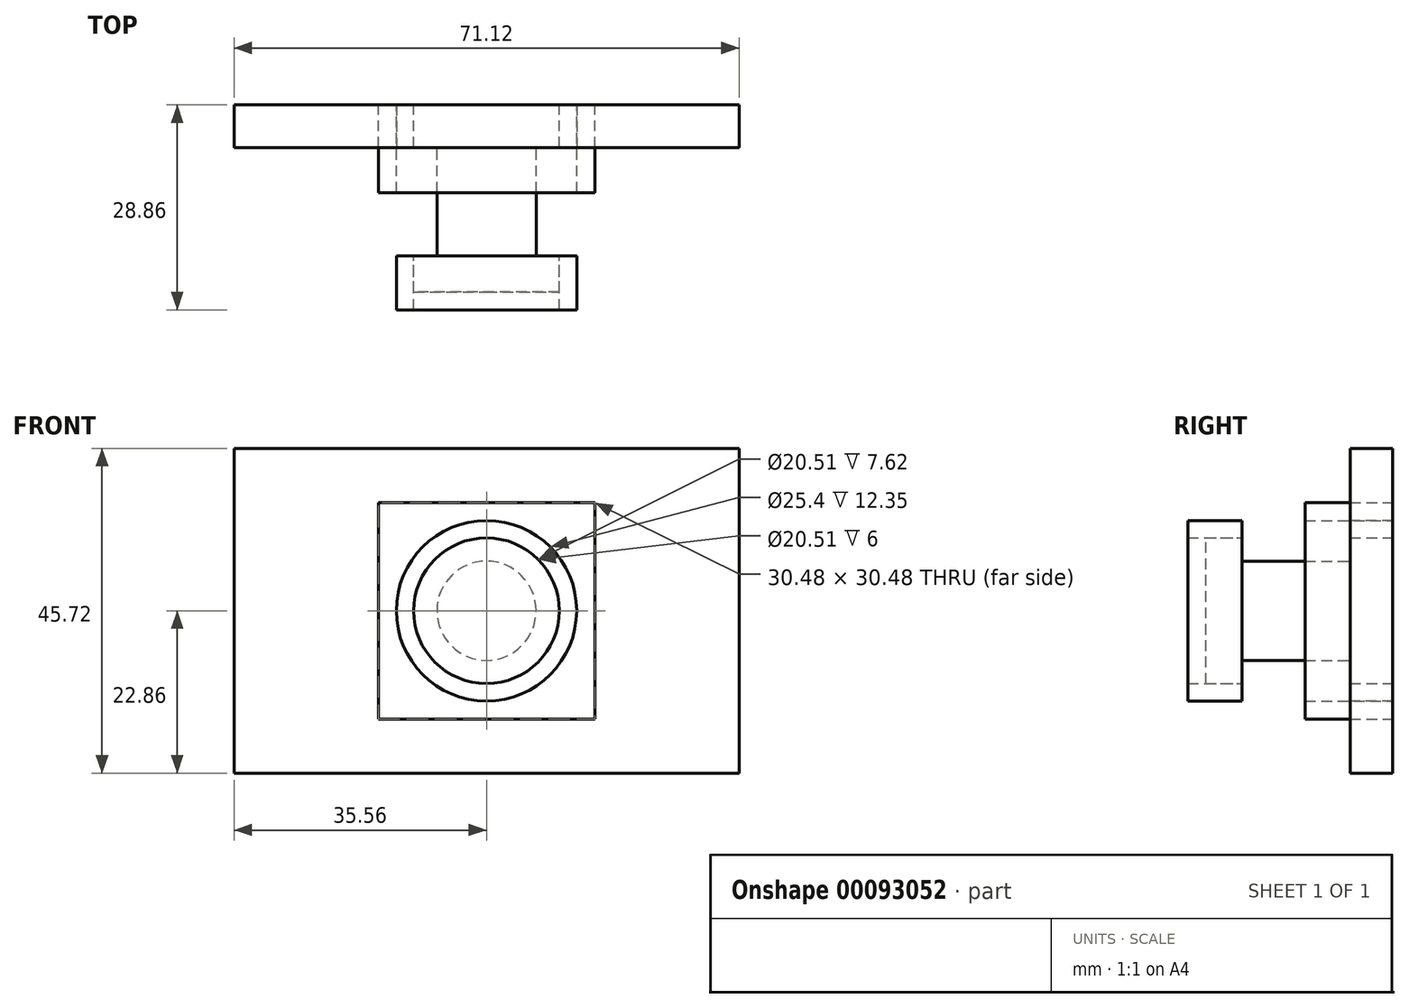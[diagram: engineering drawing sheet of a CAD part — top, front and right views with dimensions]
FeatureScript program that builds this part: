
annotation { "Feature Type Name" : "Feature", "Feature Type Description" : "" }
export const myFeature = defineFeature(function(context is Context, id is Id, definition is map)
    precondition{}
    {
        {
            var Q0;
            Q0=qCreatedBy(makeId("Front.planeOp"),FACE);
            var sketch = newSketch(context, id + "F0", { "sketchPlane" : qUnion([Q0])});
            skLineSegment(sketch, "E0.bottom", {"start": v(-35.56, -22.86) * mm, "end": v(35.56, -22.86) * mm});
            skLineSegment(sketch, "E0.top", {"start": v(-35.56, 22.86) * mm, "end": v(35.56, 22.86) * mm});
            skLineSegment(sketch, "E0.left", {"start": v(-35.56, -22.86) * mm, "end": v(-35.56, 22.86) * mm});
            skLineSegment(sketch, "E0.right", {"start": v(35.56, -22.86) * mm, "end": v(35.56, 22.86) * mm});
            skPoint(sketch, "E0.middle", {"position": v(0, 0) * mm});
            skLineSegment(sketch, "E1.bottom", {"start": v(15.24, -15.24) * mm, "end": v(-15.24, -15.24) * mm});
            skLineSegment(sketch, "E1.top", {"start": v(15.24, 15.24) * mm, "end": v(-15.24, 15.24) * mm});
            skLineSegment(sketch, "E1.left", {"start": v(15.24, -15.24) * mm, "end": v(15.24, 15.24) * mm});
            skLineSegment(sketch, "E1.right", {"start": v(-15.24, -15.24) * mm, "end": v(-15.24, 15.24) * mm});
            skCircle(sketch, "E2", {"center": v(0, 0) * mm, "radius": 10.25 * mm});
            skCircle(sketch, "E3", {"center": v(0, 0) * mm, "radius": 6.99 * mm});
            skCircle(sketch, "E4", {"center": v(0, 0) * mm, "radius": 12.7 * mm});
            skSolve(sketch);
        }
        {
            var Q0;
            Q0 = qSketchRegion(id + "F0", true);
            extrude(context, id + "F1", {"entities" : qUnion([Q0]), "oppositeDirection" : true, "depth" : 6 * mm});
        }
        {
            var Q0;
            Q0=makeQuery(id+"F0.imprint","IMPRINT",FACE,{"disambiguationData":[TD([[makeQuery(id+"F0.imprint","IMPRINT",EDGE,{"derivedFrom":sQuery(id+"F0.wireOp",EDGE,"E1.bottom")}),-1.0]])]});
            var Q1;
            {var subQ0=sQuery(id+"F0.wireOp",EDGE,"E1.right");var subQ1=sQuery(id+"F0.wireOp",EDGE,"E1.top");var subQ2=makeQuery(id+"F0.imprint","INTERSECT",VERTEX,{"derivedFrom":[subQ1,subQ0]});Q1=makeQuery(id+"F0.imprint","IMPRINT",FACE,{"disambiguationData":[TD([[makeQuery(id+"F0.imprint","IMPRINT",EDGE,{"disambiguationData":[TD([[subQ2,1.0]])],"derivedFrom":subQ1}),1.0]])]});}
            var Q2;
            {var subQ0=sQuery(id+"F0.wireOp",EDGE,"E1.left");var subQ1=sQuery(id+"F0.wireOp",EDGE,"E1.top");var subQ2=makeQuery(id+"F0.imprint","INTERSECT",VERTEX,{"derivedFrom":[subQ1,subQ0]});Q2=makeQuery(id+"F0.imprint","IMPRINT",FACE,{"disambiguationData":[TD([[makeQuery(id+"F0.imprint","IMPRINT",EDGE,{"disambiguationData":[TD([[subQ2,-1.0]])],"derivedFrom":subQ1}),1.0]])]});}
            var Q3;
            Q3=makeQuery(id+"F1.opExtrude","CAP_FACE",FACE,{"disambiguationData":[OSD([sQuery(id+"F0.wireOp",EDGE,"E0.bottom"),sQuery(id+"F0.wireOp",EDGE,"E0.top"),sQuery(id+"F0.wireOp",EDGE,"E0.left"),sQuery(id+"F0.wireOp",EDGE,"E0.right"),sQuery(id+"F0.wireOp",EDGE,"E1.bottom"),sQuery(id+"F0.wireOp",EDGE,"E1.top"),sQuery(id+"F0.wireOp",EDGE,"E1.left"),sQuery(id+"F0.wireOp",EDGE,"E1.right")])],"isStart":false});
            extrude(context, id + "F2", {"entities" : qUnion([Q0, Q1, Q2]), "depth" : 6.35 * mm, "hasSecondDirection" : true, "secondDirectionBound" : SecondDirectionBoundingType.UP_TO_SURFACE, "secondDirectionOppositeDirection" : true, "secondDirectionBoundEntityFace" : qUnion([Q3]), "secondDirectionDepth" : 25.4 * mm});
        }
        {
            var Q0;
            Q0=makeQuery(id+"F0.imprint","IMPRINT",FACE,{"disambiguationData":[TD([[makeQuery(id+"F0.imprint","IMPRINT",EDGE,{"derivedFrom":sQuery(id+"F0.wireOp",EDGE,"E2")}),1.0]])]});
            var Q1;
            Q1=makeQuery(id+"F0.imprint","IMPRINT",FACE,{"disambiguationData":[TD([[makeQuery(id+"F0.imprint","IMPRINT",EDGE,{"derivedFrom":sQuery(id+"F0.wireOp",EDGE,"E3")}),1.0]])]});
            var Q2;
            Q2=makeQuery(id+"F1.opExtrude","CAP_FACE",FACE,{"disambiguationData":[OSD([sQuery(id+"F0.wireOp",EDGE,"E0.bottom"),sQuery(id+"F0.wireOp",EDGE,"E0.top"),sQuery(id+"F0.wireOp",EDGE,"E0.left"),sQuery(id+"F0.wireOp",EDGE,"E0.right"),sQuery(id+"F0.wireOp",EDGE,"E1.bottom"),sQuery(id+"F0.wireOp",EDGE,"E1.top"),sQuery(id+"F0.wireOp",EDGE,"E1.left"),sQuery(id+"F0.wireOp",EDGE,"E1.right")])],"isStart":false});
            extrude(context, id + "F3", {"entities" : qUnion([Q0, Q1]), "depth" : 20.32 * mm, "hasSecondDirection" : true, "secondDirectionBound" : SecondDirectionBoundingType.UP_TO_SURFACE, "secondDirectionOppositeDirection" : true, "secondDirectionBoundEntityFace" : qUnion([Q2]), "secondDirectionDepth" : 25.4 * mm});
        }
        {
            var Q0;
            Q0=makeQuery(id+"F0.imprint","IMPRINT",FACE,{"disambiguationData":[TD([[makeQuery(id+"F0.imprint","IMPRINT",EDGE,{"derivedFrom":sQuery(id+"F0.wireOp",EDGE,"E2")}),1.0]])]});
            var Q1;
            Q1=makeQuery(id+"F1.opExtrude","CAP_FACE",FACE,{"disambiguationData":[OSD([sQuery(id+"F0.wireOp",EDGE,"E0.bottom"),sQuery(id+"F0.wireOp",EDGE,"E0.top"),sQuery(id+"F0.wireOp",EDGE,"E0.left"),sQuery(id+"F0.wireOp",EDGE,"E0.right"),sQuery(id+"F0.wireOp",EDGE,"E1.bottom"),sQuery(id+"F0.wireOp",EDGE,"E1.top"),sQuery(id+"F0.wireOp",EDGE,"E1.left"),sQuery(id+"F0.wireOp",EDGE,"E1.right")])],"isStart":false});
            extrude(context, id + "F4", {"entities" : qUnion([Q0]), "operationType" : NewBodyOperationType.REMOVE, "depth" : 15.24 * mm});
        }
        {
            var Q0;
            Q0=makeQuery(id+"F0.imprint","IMPRINT",FACE,{"disambiguationData":[TD([[makeQuery(id+"F0.imprint","IMPRINT",EDGE,{"derivedFrom":sQuery(id+"F0.wireOp",EDGE,"E2")}),-1.0]])]});
            extrude(context, id + "F5", {"entities" : qUnion([Q0]), "depth" : 22.86 * mm});
        }
        {
            var Q0;
            Q0=makeQuery(id+"F0.imprint","IMPRINT",FACE,{"disambiguationData":[TD([[makeQuery(id+"F0.imprint","IMPRINT",EDGE,{"derivedFrom":sQuery(id+"F0.wireOp",EDGE,"E2")}),-1.0]])]});
            extrude(context, id + "F6", {"entities" : qUnion([Q0]), "operationType" : NewBodyOperationType.REMOVE, "depth" : 15.24 * mm});
        }
        {
            var Q0;
            Q0=makeQuery(id+"F0.imprint","IMPRINT",FACE,{"disambiguationData":[TD([[makeQuery(id+"F0.imprint","IMPRINT",EDGE,{"derivedFrom":sQuery(id+"F0.wireOp",EDGE,"E2")}),-1.0]])]});
            var Q1;
            Q1=makeQuery(id+"F2.opExtrude","CAP_FACE",FACE,{"disambiguationData":[OSD([sQuery(id+"F0.wireOp",EDGE,"E1.bottom"),sQuery(id+"F0.wireOp",EDGE,"E1.top"),sQuery(id+"F0.wireOp",EDGE,"E1.left"),sQuery(id+"F0.wireOp",EDGE,"E1.right"),sQuery(id+"F0.wireOp",EDGE,"E4")])],"isStart":true});
            extrude(context, id + "F7", {"entities" : qUnion([Q0]), "endBound" : BoundingType.UP_TO_SURFACE, "oppositeDirection" : true, "endBoundEntityFace" : qUnion([Q1]), "depth" : 25.4 * mm});
        }
    });
